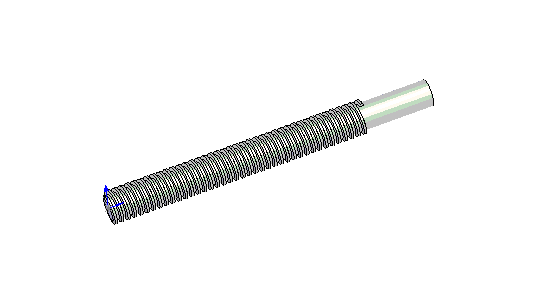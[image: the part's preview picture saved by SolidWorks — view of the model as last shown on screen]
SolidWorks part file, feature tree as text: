
SOLIDWORKS PART (.sldprt)
format: sldprt  version: not decoded by parser v0  size: 737,792 bytes
history: native  units: mm
features: sketch x3, extrude x1, helix x1, sweep x1 (+11 scaffold rows collapsed)
feature tree (17):
  scaffold x11  (default folders/planes/origin — collapsed)
  sketch  "Sketch2"  dims[c1.D1=12.7mm c1.D2=1.27mm c1.D3=~3.577275mm c2.D3=~67.850421deg c3.D3=~3.577275mm c4.D3=14.5deg c4.D4=~3.608596mm c5.D4=14.5deg c5.D5=~9.39374mm c6.D5=29.0deg c6.D6=~3.968321mm c7.D6=~14.484981deg c8.D6=~9.39374mm c9.D6=14.5deg c9.D5=~4.028361mm c10.D5=14.5deg c10.D7=2.54mm c10.D8=2.54mm c10.D9=~3.243972mm c11.D7=2.54mm c11.D8=0.635mm c11.D9=2.54mm c11.D10=2.54mm c12.D7=2.54mm c12.D10=1.27mm c12.D11=~5.014643mm c13.D11=~15.254683deg c14.D11=12.7mm c14.D12=25.4mm c14.D13=12.7mm c14.D14=6.35mm c15.D11=12.7mm c15.D15=35.0107mm c16.D15=~142.078379deg c17.D15=35.0107mm c18.D15=60.0deg c18.D16=1.27mm c18.D17=~2.213637mm c19.D17=~135.351408deg c20.D17=12.7mm c21.D17=45.0deg c21.D18=12.827mm c21.D19=1.27mm c21.D20=~2.753862mm c22.D20=45.0deg c22.D21=1.5875mm c22.D2=0.635mm c22.D4=~1.592156mm c23.D4=~0.124313deg c24.D4=1.27mm]
  sketch  "Sketch3"  dims[D1=10.16mm]
  extrude  "Extrude1"  Depth=127mm
  sketch  "Sketch4"  dims[D1=11.43mm]
  helix  "Helix1"  Pitch=101.6mm
  sweep  "Sweep1"
decode coverage: 5 of 6 modeling features carry decoded parameters
note: ~ marks probable driven/reference dimensions
note: suppression state not decoded; provenance and decode notes live in map.json
